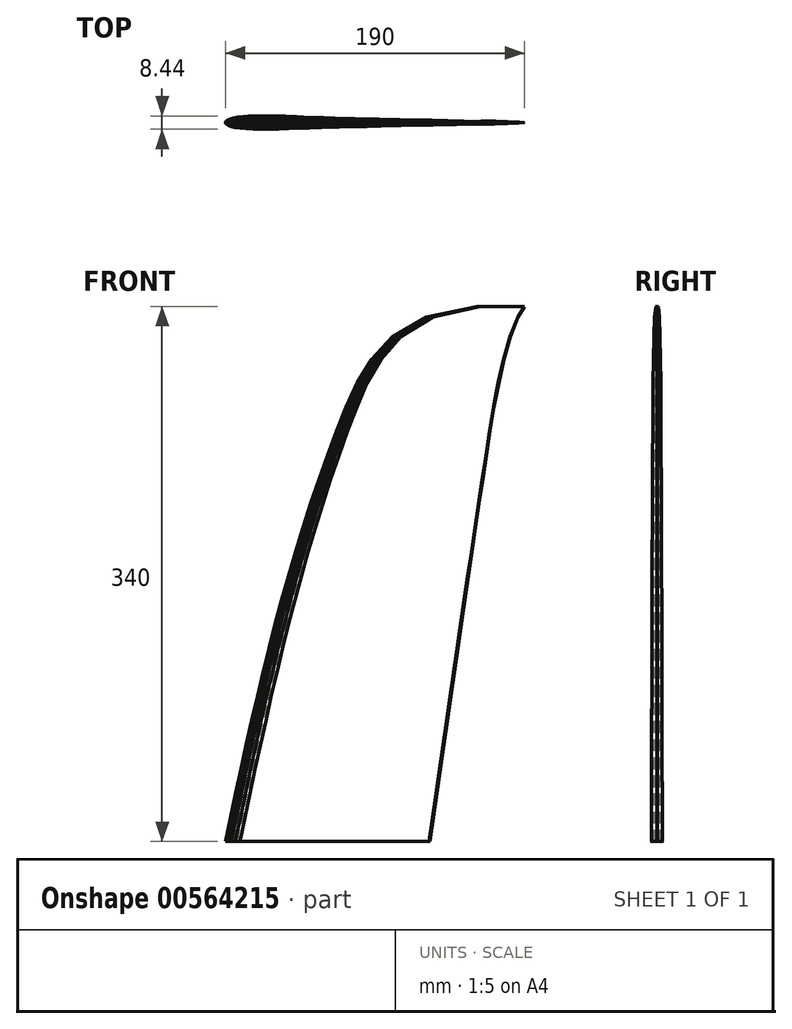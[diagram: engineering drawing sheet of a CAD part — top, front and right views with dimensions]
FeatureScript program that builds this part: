
annotation { "Feature Type Name" : "Feature", "Feature Type Description" : "" }
export const myFeature = defineFeature(function(context is Context, id is Id, definition is map)
    precondition{}
    {
        {
            var Q0;
            Q0=qCreatedBy(makeId("Top.planeOp"),FACE);
            cPlane(context, id + "F0", {"entities" : qUnion([Q0]), "cplaneType" : CPlaneType.OFFSET, "offset" : 250 * mm, "width" : 150 * mm, "height" : 150 * mm});
        }
        {
            var Q0;
            Q0=qCreatedBy(makeId("Top.planeOp"),FACE);
            cPlane(context, id + "F1", {"entities" : qUnion([Q0]), "cplaneType" : CPlaneType.OFFSET, "offset" : 300 * mm, "width" : 150 * mm, "height" : 150 * mm});
        }
        {
            var Q0;
            Q0=qCreatedBy(makeId("Top.planeOp"),FACE);
            cPlane(context, id + "F2", {"entities" : qUnion([Q0]), "cplaneType" : CPlaneType.OFFSET, "offset" : 320 * mm, "width" : 150 * mm, "height" : 150 * mm});
        }
        {
            var Q0;
            Q0=qCreatedBy(makeId("Top.planeOp"),FACE);
            cPlane(context, id + "F3", {"entities" : qUnion([Q0]), "cplaneType" : CPlaneType.OFFSET, "offset" : 340 * mm, "width" : 150 * mm, "height" : 150 * mm});
        }
        {
            var Q0;
            Q0=qCreatedBy(makeId("Top.planeOp"),FACE);
            var sketch = newSketch(context, id + "F4", { "sketchPlane" : qUnion([Q0])});
            skLineSegment(sketch, "E0", {"start": v(130, 0.16) * mm, "end": v(129.46, 0.15) * mm});
            skLineSegment(sketch, "E1", {"start": v(129.46, 0.15) * mm, "end": v(128.28, 0.22) * mm});
            skLineSegment(sketch, "E2", {"start": v(128.28, 0.22) * mm, "end": v(126.06, 0.3) * mm});
            skLineSegment(sketch, "E3", {"start": v(126.06, 0.3) * mm, "end": v(123.2, 0.44) * mm});
            skLineSegment(sketch, "E4", {"start": v(123.2, 0.44) * mm, "end": v(119.45, 0.6) * mm});
            skLineSegment(sketch, "E5", {"start": v(119.45, 0.6) * mm, "end": v(115.33, 0.75) * mm});
            skLineSegment(sketch, "E6", {"start": v(115.33, 0.75) * mm, "end": v(110.89, 0.96) * mm});
            skLineSegment(sketch, "E7", {"start": v(110.89, 0.96) * mm, "end": v(106, 1.14) * mm});
            skLineSegment(sketch, "E8", {"start": v(106, 1.14) * mm, "end": v(100.37, 1.42) * mm});
            skLineSegment(sketch, "E9", {"start": v(100.37, 1.42) * mm, "end": v(94.84, 1.6) * mm});
            skLineSegment(sketch, "E10", {"start": v(94.84, 1.6) * mm, "end": v(89.05, 1.89) * mm});
            skLineSegment(sketch, "E11", {"start": v(89.05, 1.89) * mm, "end": v(82.47, 2.15) * mm});
            skLineSegment(sketch, "E12", {"start": v(82.47, 2.15) * mm, "end": v(76.13, 2.4) * mm});
            skLineSegment(sketch, "E13", {"start": v(76.13, 2.4) * mm, "end": v(69.53, 2.68) * mm});
            skLineSegment(sketch, "E14", {"start": v(69.53, 2.68) * mm, "end": v(62.6, 3.03) * mm});
            skLineSegment(sketch, "E15", {"start": v(62.6, 3.03) * mm, "end": v(56.55, 3.26) * mm});
            skLineSegment(sketch, "E16", {"start": v(56.55, 3.26) * mm, "end": v(49.78, 3.57) * mm});
            skLineSegment(sketch, "E17", {"start": v(49.78, 3.57) * mm, "end": v(45.16, 3.74) * mm});
            skLineSegment(sketch, "E18", {"start": v(45.16, 3.74) * mm, "end": v(38.39, 3.98) * mm});
            skLineSegment(sketch, "E19", {"start": v(38.39, 3.98) * mm, "end": v(33.66, 4.1) * mm});
            skLineSegment(sketch, "E20", {"start": v(33.66, 4.1) * mm, "end": v(28.01, 4.2) * mm});
            skLineSegment(sketch, "E21", {"start": v(28.01, 4.2) * mm, "end": v(23.16, 4.22) * mm});
            skLineSegment(sketch, "E22", {"start": v(23.16, 4.22) * mm, "end": v(18.3, 4.15) * mm});
            skLineSegment(sketch, "E23", {"start": v(18.3, 4.15) * mm, "end": v(14.57, 4) * mm});
            skLineSegment(sketch, "E24", {"start": v(14.57, 4) * mm, "end": v(11.21, 3.75) * mm});
            skLineSegment(sketch, "E25", {"start": v(11.21, 3.75) * mm, "end": v(7.63, 3.34) * mm});
            skLineSegment(sketch, "E26", {"start": v(7.63, 3.34) * mm, "end": v(5.05, 2.89) * mm});
            skLineSegment(sketch, "E27", {"start": v(5.05, 2.89) * mm, "end": v(2.92, 2.28) * mm});
            skLineSegment(sketch, "E28", {"start": v(2.92, 2.28) * mm, "end": v(1.32, 1.56) * mm});
            skLineSegment(sketch, "E29", {"start": v(1.32, 1.56) * mm, "end": v(0.49, 0.98) * mm});
            skLineSegment(sketch, "E30", {"start": v(0.49, 0.98) * mm, "end": v(0.08, 0.4) * mm});
            skLineSegment(sketch, "E31", {"start": v(0.08, 0.4) * mm, "end": v(0, 0) * mm});
            skLineSegment(sketch, "E32", {"start": v(0, 0) * mm, "end": v(0.03, -0.22) * mm});
            skLineSegment(sketch, "E33", {"start": v(0.03, -0.22) * mm, "end": v(0.08, -0.45) * mm});
            skLineSegment(sketch, "E34", {"start": v(0.08, -0.45) * mm, "end": v(0.22, -0.67) * mm});
            skLineSegment(sketch, "E35", {"start": v(0.22, -0.67) * mm, "end": v(1, -1.38) * mm});
            skLineSegment(sketch, "E36", {"start": v(1, -1.38) * mm, "end": v(2.07, -1.93) * mm});
            skLineSegment(sketch, "E37", {"start": v(2.07, -1.93) * mm, "end": v(3.73, -2.53) * mm});
            skLineSegment(sketch, "E38", {"start": v(3.73, -2.53) * mm, "end": v(6.34, -3.13) * mm});
            skLineSegment(sketch, "E39", {"start": v(6.34, -3.13) * mm, "end": v(9.36, -3.57) * mm});
            skLineSegment(sketch, "E40", {"start": v(9.36, -3.57) * mm, "end": v(13.18, -3.91) * mm});
            skLineSegment(sketch, "E41", {"start": v(13.18, -3.91) * mm, "end": v(17.57, -4.14) * mm});
            skLineSegment(sketch, "E42", {"start": v(17.57, -4.14) * mm, "end": v(22.67, -4.2) * mm});
            skLineSegment(sketch, "E43", {"start": v(22.67, -4.2) * mm, "end": v(28.18, -4.22) * mm});
            skLineSegment(sketch, "E44", {"start": v(28.18, -4.22) * mm, "end": v(34.02, -4.06) * mm});
            skLineSegment(sketch, "E45", {"start": v(34.02, -4.06) * mm, "end": v(40.18, -3.88) * mm});
            skLineSegment(sketch, "E46", {"start": v(40.18, -3.88) * mm, "end": v(46.73, -3.67) * mm});
            skLineSegment(sketch, "E47", {"start": v(46.73, -3.67) * mm, "end": v(53.52, -3.4) * mm});
            skLineSegment(sketch, "E48", {"start": v(53.52, -3.4) * mm, "end": v(61.2, -3.04) * mm});
            skLineSegment(sketch, "E49", {"start": v(61.2, -3.04) * mm, "end": v(67.7, -2.76) * mm});
            skLineSegment(sketch, "E50", {"start": v(67.7, -2.76) * mm, "end": v(74.25, -2.49) * mm});
            skLineSegment(sketch, "E51", {"start": v(74.25, -2.49) * mm, "end": v(81.45, -2.17) * mm});
            skLineSegment(sketch, "E52", {"start": v(81.45, -2.17) * mm, "end": v(88.16, -1.9) * mm});
            skLineSegment(sketch, "E53", {"start": v(88.16, -1.9) * mm, "end": v(94.61, -1.62) * mm});
            skLineSegment(sketch, "E54", {"start": v(94.61, -1.62) * mm, "end": v(100.76, -1.37) * mm});
            skLineSegment(sketch, "E55", {"start": v(100.76, -1.37) * mm, "end": v(106.42, -1.13) * mm});
            skLineSegment(sketch, "E56", {"start": v(106.42, -1.13) * mm, "end": v(111.7, -0.9) * mm});
            skLineSegment(sketch, "E57", {"start": v(111.7, -0.9) * mm, "end": v(116.1, -0.72) * mm});
            skLineSegment(sketch, "E58", {"start": v(116.1, -0.72) * mm, "end": v(120.1, -0.54) * mm});
            skLineSegment(sketch, "E59", {"start": v(120.1, -0.54) * mm, "end": v(123.41, -0.43) * mm});
            skLineSegment(sketch, "E60", {"start": v(123.41, -0.43) * mm, "end": v(126.23, -0.29) * mm});
            skLineSegment(sketch, "E61", {"start": v(126.23, -0.29) * mm, "end": v(128.2, -0.2) * mm});
            skLineSegment(sketch, "E62", {"start": v(128.2, -0.2) * mm, "end": v(130, -0.13) * mm});
            skLineSegment(sketch, "E63", {"start": v(130, -0.13) * mm, "end": v(130, 0.16) * mm});
            skSolve(sketch);
        }
        {
            var Q0;
            Q0=qCreatedBy(id+"F0.planeOp",FACE);
            var sketch = newSketch(context, id + "F5", { "sketchPlane" : qUnion([Q0])});
            skLineSegment(sketch, "E64", {"start": v(166.6, 0.13) * mm, "end": v(166.18, 0.12) * mm});
            skLineSegment(sketch, "E65", {"start": v(166.18, 0.12) * mm, "end": v(165.27, 0.17) * mm});
            skLineSegment(sketch, "E66", {"start": v(165.27, 0.17) * mm, "end": v(163.56, 0.23) * mm});
            skLineSegment(sketch, "E67", {"start": v(163.56, 0.23) * mm, "end": v(161.37, 0.33) * mm});
            skLineSegment(sketch, "E68", {"start": v(161.37, 0.33) * mm, "end": v(158.49, 0.46) * mm});
            skLineSegment(sketch, "E69", {"start": v(158.49, 0.46) * mm, "end": v(155.31, 0.58) * mm});
            skLineSegment(sketch, "E70", {"start": v(155.31, 0.58) * mm, "end": v(151.9, 0.74) * mm});
            skLineSegment(sketch, "E71", {"start": v(151.9, 0.74) * mm, "end": v(148.14, 0.88) * mm});
            skLineSegment(sketch, "E72", {"start": v(148.14, 0.88) * mm, "end": v(143.8, 1.1) * mm});
            skLineSegment(sketch, "E73", {"start": v(143.8, 1.1) * mm, "end": v(139.55, 1.24) * mm});
            skLineSegment(sketch, "E74", {"start": v(139.55, 1.24) * mm, "end": v(135.1, 1.45) * mm});
            skLineSegment(sketch, "E75", {"start": v(135.1, 1.45) * mm, "end": v(130.04, 1.65) * mm});
            skLineSegment(sketch, "E76", {"start": v(130.04, 1.65) * mm, "end": v(125.16, 1.85) * mm});
            skLineSegment(sketch, "E77", {"start": v(125.16, 1.85) * mm, "end": v(120.08, 2.06) * mm});
            skLineSegment(sketch, "E78", {"start": v(120.08, 2.06) * mm, "end": v(114.76, 2.33) * mm});
            skLineSegment(sketch, "E79", {"start": v(114.76, 2.33) * mm, "end": v(110.1, 2.5) * mm});
            skLineSegment(sketch, "E80", {"start": v(110.1, 2.5) * mm, "end": v(104.9, 2.75) * mm});
            skLineSegment(sketch, "E81", {"start": v(104.9, 2.75) * mm, "end": v(101.34, 2.88) * mm});
            skLineSegment(sketch, "E82", {"start": v(101.34, 2.88) * mm, "end": v(96.13, 3.06) * mm});
            skLineSegment(sketch, "E83", {"start": v(96.13, 3.06) * mm, "end": v(92.5, 3.16) * mm});
            skLineSegment(sketch, "E84", {"start": v(92.5, 3.16) * mm, "end": v(88.15, 3.23) * mm});
            skLineSegment(sketch, "E85", {"start": v(88.15, 3.23) * mm, "end": v(84.42, 3.24) * mm});
            skLineSegment(sketch, "E86", {"start": v(84.42, 3.24) * mm, "end": v(80.69, 3.19) * mm});
            skLineSegment(sketch, "E87", {"start": v(80.69, 3.19) * mm, "end": v(77.81, 3.08) * mm});
            skLineSegment(sketch, "E88", {"start": v(77.81, 3.08) * mm, "end": v(75.23, 2.89) * mm});
            skLineSegment(sketch, "E89", {"start": v(75.23, 2.89) * mm, "end": v(72.47, 2.57) * mm});
            skLineSegment(sketch, "E90", {"start": v(72.47, 2.57) * mm, "end": v(70.5, 2.22) * mm});
            skLineSegment(sketch, "E91", {"start": v(70.5, 2.22) * mm, "end": v(68.85, 1.76) * mm});
            skLineSegment(sketch, "E92", {"start": v(68.85, 1.76) * mm, "end": v(67.62, 1.2) * mm});
            skLineSegment(sketch, "E93", {"start": v(67.62, 1.2) * mm, "end": v(66.98, 0.75) * mm});
            skLineSegment(sketch, "E94", {"start": v(66.98, 0.75) * mm, "end": v(66.66, 0.3) * mm});
            skLineSegment(sketch, "E95", {"start": v(66.66, 0.3) * mm, "end": v(66.6, 0) * mm});
            skLineSegment(sketch, "E96", {"start": v(66.6, 0) * mm, "end": v(66.62, -0.17) * mm});
            skLineSegment(sketch, "E97", {"start": v(66.62, -0.17) * mm, "end": v(66.66, -0.35) * mm});
            skLineSegment(sketch, "E98", {"start": v(66.66, -0.35) * mm, "end": v(66.78, -0.52) * mm});
            skLineSegment(sketch, "E99", {"start": v(66.78, -0.52) * mm, "end": v(67.37, -1.06) * mm});
            skLineSegment(sketch, "E100", {"start": v(67.37, -1.06) * mm, "end": v(68.2, -1.48) * mm});
            skLineSegment(sketch, "E101", {"start": v(68.2, -1.48) * mm, "end": v(69.47, -1.95) * mm});
            skLineSegment(sketch, "E102", {"start": v(69.47, -1.95) * mm, "end": v(71.48, -2.4) * mm});
            skLineSegment(sketch, "E103", {"start": v(71.48, -2.4) * mm, "end": v(73.8, -2.74) * mm});
            skLineSegment(sketch, "E104", {"start": v(73.8, -2.74) * mm, "end": v(76.75, -3) * mm});
            skLineSegment(sketch, "E105", {"start": v(76.75, -3) * mm, "end": v(80.12, -3.18) * mm});
            skLineSegment(sketch, "E106", {"start": v(80.12, -3.18) * mm, "end": v(84.04, -3.23) * mm});
            skLineSegment(sketch, "E107", {"start": v(84.04, -3.23) * mm, "end": v(88.28, -3.24) * mm});
            skLineSegment(sketch, "E108", {"start": v(88.28, -3.24) * mm, "end": v(92.77, -3.12) * mm});
            skLineSegment(sketch, "E109", {"start": v(92.77, -3.12) * mm, "end": v(97.5, -2.99) * mm});
            skLineSegment(sketch, "E110", {"start": v(97.5, -2.99) * mm, "end": v(102.55, -2.82) * mm});
            skLineSegment(sketch, "E111", {"start": v(102.55, -2.82) * mm, "end": v(107.77, -2.62) * mm});
            skLineSegment(sketch, "E112", {"start": v(107.77, -2.62) * mm, "end": v(113.67, -2.34) * mm});
            skLineSegment(sketch, "E113", {"start": v(113.67, -2.34) * mm, "end": v(118.68, -2.12) * mm});
            skLineSegment(sketch, "E114", {"start": v(118.68, -2.12) * mm, "end": v(123.72, -1.91) * mm});
            skLineSegment(sketch, "E115", {"start": v(123.72, -1.91) * mm, "end": v(129.25, -1.67) * mm});
            skLineSegment(sketch, "E116", {"start": v(129.25, -1.67) * mm, "end": v(134.41, -1.46) * mm});
            skLineSegment(sketch, "E117", {"start": v(134.41, -1.46) * mm, "end": v(139.38, -1.24) * mm});
            skLineSegment(sketch, "E118", {"start": v(139.38, -1.24) * mm, "end": v(144.1, -1.06) * mm});
            skLineSegment(sketch, "E119", {"start": v(144.1, -1.06) * mm, "end": v(148.46, -0.87) * mm});
            skLineSegment(sketch, "E120", {"start": v(148.46, -0.87) * mm, "end": v(152.52, -0.7) * mm});
            skLineSegment(sketch, "E121", {"start": v(152.52, -0.7) * mm, "end": v(155.91, -0.56) * mm});
            skLineSegment(sketch, "E122", {"start": v(155.91, -0.56) * mm, "end": v(158.99, -0.42) * mm});
            skLineSegment(sketch, "E123", {"start": v(158.99, -0.42) * mm, "end": v(161.53, -0.33) * mm});
            skLineSegment(sketch, "E124", {"start": v(161.53, -0.33) * mm, "end": v(163.7, -0.22) * mm});
            skLineSegment(sketch, "E125", {"start": v(163.7, -0.22) * mm, "end": v(165.2, -0.15) * mm});
            skLineSegment(sketch, "E126", {"start": v(165.2, -0.15) * mm, "end": v(166.6, -0.1) * mm});
            skLineSegment(sketch, "E127", {"start": v(166.6, -0.1) * mm, "end": v(166.6, 0.13) * mm});
            skSolve(sketch);
        }
        {
            var Q0;
            Q0=qCreatedBy(id+"F1.planeOp",FACE);
            var sketch = newSketch(context, id + "F6", { "sketchPlane" : qUnion([Q0])});
            skLineSegment(sketch, "E128", {"start": v(175.53, 0.1) * mm, "end": v(175.16, 0.1) * mm});
            skLineSegment(sketch, "E129", {"start": v(175.16, 0.1) * mm, "end": v(174.37, 0.15) * mm});
            skLineSegment(sketch, "E130", {"start": v(174.37, 0.15) * mm, "end": v(172.88, 0.2) * mm});
            skLineSegment(sketch, "E131", {"start": v(172.88, 0.2) * mm, "end": v(170.98, 0.3) * mm});
            skLineSegment(sketch, "E132", {"start": v(170.98, 0.3) * mm, "end": v(168.46, 0.4) * mm});
            skLineSegment(sketch, "E133", {"start": v(168.46, 0.4) * mm, "end": v(165.7, 0.5) * mm});
            skLineSegment(sketch, "E134", {"start": v(165.7, 0.5) * mm, "end": v(162.73, 0.64) * mm});
            skLineSegment(sketch, "E135", {"start": v(162.73, 0.64) * mm, "end": v(159.46, 0.76) * mm});
            skLineSegment(sketch, "E136", {"start": v(159.46, 0.76) * mm, "end": v(155.68, 0.95) * mm});
            skLineSegment(sketch, "E137", {"start": v(155.68, 0.95) * mm, "end": v(151.98, 1.08) * mm});
            skLineSegment(sketch, "E138", {"start": v(151.98, 1.08) * mm, "end": v(148.1, 1.26) * mm});
            skLineSegment(sketch, "E139", {"start": v(148.1, 1.26) * mm, "end": v(143.7, 1.44) * mm});
            skLineSegment(sketch, "E140", {"start": v(143.7, 1.44) * mm, "end": v(139.45, 1.61) * mm});
            skLineSegment(sketch, "E141", {"start": v(139.45, 1.61) * mm, "end": v(135.03, 1.8) * mm});
            skLineSegment(sketch, "E142", {"start": v(135.03, 1.8) * mm, "end": v(130.4, 2.03) * mm});
            skLineSegment(sketch, "E143", {"start": v(130.4, 2.03) * mm, "end": v(126.34, 2.18) * mm});
            skLineSegment(sketch, "E144", {"start": v(126.34, 2.18) * mm, "end": v(121.81, 2.4) * mm});
            skLineSegment(sketch, "E145", {"start": v(121.81, 2.4) * mm, "end": v(118.72, 2.5) * mm});
            skLineSegment(sketch, "E146", {"start": v(118.72, 2.5) * mm, "end": v(114.18, 2.66) * mm});
            skLineSegment(sketch, "E147", {"start": v(114.18, 2.66) * mm, "end": v(111.02, 2.75) * mm});
            skLineSegment(sketch, "E148", {"start": v(111.02, 2.75) * mm, "end": v(107.23, 2.81) * mm});
            skLineSegment(sketch, "E149", {"start": v(107.23, 2.81) * mm, "end": v(103.99, 2.82) * mm});
            skLineSegment(sketch, "E150", {"start": v(103.99, 2.82) * mm, "end": v(100.74, 2.78) * mm});
            skLineSegment(sketch, "E151", {"start": v(100.74, 2.78) * mm, "end": v(98.23, 2.68) * mm});
            skLineSegment(sketch, "E152", {"start": v(98.23, 2.68) * mm, "end": v(95.99, 2.51) * mm});
            skLineSegment(sketch, "E153", {"start": v(95.99, 2.51) * mm, "end": v(93.58, 2.24) * mm});
            skLineSegment(sketch, "E154", {"start": v(93.58, 2.24) * mm, "end": v(91.86, 1.93) * mm});
            skLineSegment(sketch, "E155", {"start": v(91.86, 1.93) * mm, "end": v(90.43, 1.53) * mm});
            skLineSegment(sketch, "E156", {"start": v(90.43, 1.53) * mm, "end": v(89.36, 1.04) * mm});
            skLineSegment(sketch, "E157", {"start": v(89.36, 1.04) * mm, "end": v(88.8, 0.65) * mm});
            skLineSegment(sketch, "E158", {"start": v(88.8, 0.65) * mm, "end": v(88.53, 0.27) * mm});
            skLineSegment(sketch, "E159", {"start": v(88.53, 0.27) * mm, "end": v(88.47, 0) * mm});
            skLineSegment(sketch, "E160", {"start": v(88.47, 0) * mm, "end": v(88.5, -0.15) * mm});
            skLineSegment(sketch, "E161", {"start": v(88.5, -0.15) * mm, "end": v(88.53, -0.3) * mm});
            skLineSegment(sketch, "E162", {"start": v(88.53, -0.3) * mm, "end": v(88.63, -0.45) * mm});
            skLineSegment(sketch, "E163", {"start": v(88.63, -0.45) * mm, "end": v(89.14, -0.93) * mm});
            skLineSegment(sketch, "E164", {"start": v(89.14, -0.93) * mm, "end": v(89.86, -1.3) * mm});
            skLineSegment(sketch, "E165", {"start": v(89.86, -1.3) * mm, "end": v(90.98, -1.7) * mm});
            skLineSegment(sketch, "E166", {"start": v(90.98, -1.7) * mm, "end": v(92.72, -2.1) * mm});
            skLineSegment(sketch, "E167", {"start": v(92.72, -2.1) * mm, "end": v(94.75, -2.39) * mm});
            skLineSegment(sketch, "E168", {"start": v(94.75, -2.39) * mm, "end": v(97.3, -2.62) * mm});
            skLineSegment(sketch, "E169", {"start": v(97.3, -2.62) * mm, "end": v(100.24, -2.77) * mm});
            skLineSegment(sketch, "E170", {"start": v(100.24, -2.77) * mm, "end": v(103.66, -2.8) * mm});
            skLineSegment(sketch, "E171", {"start": v(103.66, -2.8) * mm, "end": v(107.34, -2.82) * mm});
            skLineSegment(sketch, "E172", {"start": v(107.34, -2.82) * mm, "end": v(111.26, -2.72) * mm});
            skLineSegment(sketch, "E173", {"start": v(111.26, -2.72) * mm, "end": v(115.38, -2.6) * mm});
            skLineSegment(sketch, "E174", {"start": v(115.38, -2.6) * mm, "end": v(119.77, -2.46) * mm});
            skLineSegment(sketch, "E175", {"start": v(119.77, -2.46) * mm, "end": v(124.31, -2.28) * mm});
            skLineSegment(sketch, "E176", {"start": v(124.31, -2.28) * mm, "end": v(129.45, -2.03) * mm});
            skLineSegment(sketch, "E177", {"start": v(129.45, -2.03) * mm, "end": v(133.81, -1.85) * mm});
            skLineSegment(sketch, "E178", {"start": v(133.81, -1.85) * mm, "end": v(138.2, -1.66) * mm});
            skLineSegment(sketch, "E179", {"start": v(138.2, -1.66) * mm, "end": v(143.02, -1.45) * mm});
            skLineSegment(sketch, "E180", {"start": v(143.02, -1.45) * mm, "end": v(147.5, -1.28) * mm});
            skLineSegment(sketch, "E181", {"start": v(147.5, -1.28) * mm, "end": v(151.83, -1.08) * mm});
            skLineSegment(sketch, "E182", {"start": v(151.83, -1.08) * mm, "end": v(155.95, -0.92) * mm});
            skLineSegment(sketch, "E183", {"start": v(155.95, -0.92) * mm, "end": v(159.74, -0.76) * mm});
            skLineSegment(sketch, "E184", {"start": v(159.74, -0.76) * mm, "end": v(163.27, -0.6) * mm});
            skLineSegment(sketch, "E185", {"start": v(163.27, -0.6) * mm, "end": v(166.22, -0.48) * mm});
            skLineSegment(sketch, "E186", {"start": v(166.22, -0.48) * mm, "end": v(168.9, -0.36) * mm});
            skLineSegment(sketch, "E187", {"start": v(168.9, -0.36) * mm, "end": v(171.11, -0.29) * mm});
            skLineSegment(sketch, "E188", {"start": v(171.11, -0.29) * mm, "end": v(173, -0.2) * mm});
            skLineSegment(sketch, "E189", {"start": v(173, -0.2) * mm, "end": v(174.32, -0.13) * mm});
            skLineSegment(sketch, "E190", {"start": v(174.32, -0.13) * mm, "end": v(175.53, -0.09) * mm});
            skLineSegment(sketch, "E191", {"start": v(175.53, -0.09) * mm, "end": v(175.53, 0.1) * mm});
            skSolve(sketch);
        }
        {
            var Q0;
            Q0=qCreatedBy(id+"F2.planeOp",FACE);
            var sketch = newSketch(context, id + "F7", { "sketchPlane" : qUnion([Q0])});
            skLineSegment(sketch, "E192", {"start": v(180.66, 0.1) * mm, "end": v(180.34, 0.09) * mm});
            skLineSegment(sketch, "E193", {"start": v(180.34, 0.09) * mm, "end": v(179.66, 0.13) * mm});
            skLineSegment(sketch, "E194", {"start": v(179.66, 0.13) * mm, "end": v(178.37, 0.17) * mm});
            skLineSegment(sketch, "E195", {"start": v(178.37, 0.17) * mm, "end": v(176.72, 0.25) * mm});
            skLineSegment(sketch, "E196", {"start": v(176.72, 0.25) * mm, "end": v(174.55, 0.34) * mm});
            skLineSegment(sketch, "E197", {"start": v(174.55, 0.34) * mm, "end": v(172.16, 0.44) * mm});
            skLineSegment(sketch, "E198", {"start": v(172.16, 0.44) * mm, "end": v(169.58, 0.55) * mm});
            skLineSegment(sketch, "E199", {"start": v(169.58, 0.55) * mm, "end": v(166.75, 0.66) * mm});
            skLineSegment(sketch, "E200", {"start": v(166.75, 0.66) * mm, "end": v(163.49, 0.82) * mm});
            skLineSegment(sketch, "E201", {"start": v(163.49, 0.82) * mm, "end": v(160.28, 0.93) * mm});
            skLineSegment(sketch, "E202", {"start": v(160.28, 0.93) * mm, "end": v(156.93, 1.1) * mm});
            skLineSegment(sketch, "E203", {"start": v(156.93, 1.1) * mm, "end": v(153.12, 1.25) * mm});
            skLineSegment(sketch, "E204", {"start": v(153.12, 1.25) * mm, "end": v(149.45, 1.4) * mm});
            skLineSegment(sketch, "E205", {"start": v(149.45, 1.4) * mm, "end": v(145.62, 1.55) * mm});
            skLineSegment(sketch, "E206", {"start": v(145.62, 1.55) * mm, "end": v(141.61, 1.76) * mm});
            skLineSegment(sketch, "E207", {"start": v(141.61, 1.76) * mm, "end": v(138.1, 1.89) * mm});
            skLineSegment(sketch, "E208", {"start": v(138.1, 1.89) * mm, "end": v(134.19, 2.07) * mm});
            skLineSegment(sketch, "E209", {"start": v(134.19, 2.07) * mm, "end": v(131.5, 2.17) * mm});
            skLineSegment(sketch, "E210", {"start": v(131.5, 2.17) * mm, "end": v(127.58, 2.3) * mm});
            skLineSegment(sketch, "E211", {"start": v(127.58, 2.3) * mm, "end": v(124.85, 2.38) * mm});
            skLineSegment(sketch, "E212", {"start": v(124.85, 2.38) * mm, "end": v(121.57, 2.43) * mm});
            skLineSegment(sketch, "E213", {"start": v(121.57, 2.43) * mm, "end": v(118.76, 2.44) * mm});
            skLineSegment(sketch, "E214", {"start": v(118.76, 2.44) * mm, "end": v(115.95, 2.4) * mm});
            skLineSegment(sketch, "E215", {"start": v(115.95, 2.4) * mm, "end": v(113.79, 2.32) * mm});
            skLineSegment(sketch, "E216", {"start": v(113.79, 2.32) * mm, "end": v(111.84, 2.17) * mm});
            skLineSegment(sketch, "E217", {"start": v(111.84, 2.17) * mm, "end": v(109.76, 1.93) * mm});
            skLineSegment(sketch, "E218", {"start": v(109.76, 1.93) * mm, "end": v(108.27, 1.67) * mm});
            skLineSegment(sketch, "E219", {"start": v(108.27, 1.67) * mm, "end": v(107.04, 1.32) * mm});
            skLineSegment(sketch, "E220", {"start": v(107.04, 1.32) * mm, "end": v(106.1, 0.9) * mm});
            skLineSegment(sketch, "E221", {"start": v(106.1, 0.9) * mm, "end": v(105.63, 0.57) * mm});
            skLineSegment(sketch, "E222", {"start": v(105.63, 0.57) * mm, "end": v(105.39, 0.23) * mm});
            skLineSegment(sketch, "E223", {"start": v(105.39, 0.23) * mm, "end": v(105.34, 0) * mm});
            skLineSegment(sketch, "E224", {"start": v(105.34, 0) * mm, "end": v(105.36, -0.13) * mm});
            skLineSegment(sketch, "E225", {"start": v(105.36, -0.13) * mm, "end": v(105.39, -0.26) * mm});
            skLineSegment(sketch, "E226", {"start": v(105.39, -0.26) * mm, "end": v(105.47, -0.39) * mm});
            skLineSegment(sketch, "E227", {"start": v(105.47, -0.39) * mm, "end": v(105.92, -0.8) * mm});
            skLineSegment(sketch, "E228", {"start": v(105.92, -0.8) * mm, "end": v(106.54, -1.12) * mm});
            skLineSegment(sketch, "E229", {"start": v(106.54, -1.12) * mm, "end": v(107.5, -1.47) * mm});
            skLineSegment(sketch, "E230", {"start": v(107.5, -1.47) * mm, "end": v(109.02, -1.81) * mm});
            skLineSegment(sketch, "E231", {"start": v(109.02, -1.81) * mm, "end": v(110.77, -2.07) * mm});
            skLineSegment(sketch, "E232", {"start": v(110.77, -2.07) * mm, "end": v(112.98, -2.27) * mm});
            skLineSegment(sketch, "E233", {"start": v(112.98, -2.27) * mm, "end": v(115.52, -2.4) * mm});
            skLineSegment(sketch, "E234", {"start": v(115.52, -2.4) * mm, "end": v(118.48, -2.43) * mm});
            skLineSegment(sketch, "E235", {"start": v(118.48, -2.43) * mm, "end": v(121.67, -2.44) * mm});
            skLineSegment(sketch, "E236", {"start": v(121.67, -2.44) * mm, "end": v(125.06, -2.35) * mm});
            skLineSegment(sketch, "E237", {"start": v(125.06, -2.35) * mm, "end": v(128.62, -2.25) * mm});
            skLineSegment(sketch, "E238", {"start": v(128.62, -2.25) * mm, "end": v(132.42, -2.13) * mm});
            skLineSegment(sketch, "E239", {"start": v(132.42, -2.13) * mm, "end": v(136.35, -1.97) * mm});
            skLineSegment(sketch, "E240", {"start": v(136.35, -1.97) * mm, "end": v(140.8, -1.76) * mm});
            skLineSegment(sketch, "E241", {"start": v(140.8, -1.76) * mm, "end": v(144.57, -1.6) * mm});
            skLineSegment(sketch, "E242", {"start": v(144.57, -1.6) * mm, "end": v(148.36, -1.44) * mm});
            skLineSegment(sketch, "E243", {"start": v(148.36, -1.44) * mm, "end": v(152.53, -1.26) * mm});
            skLineSegment(sketch, "E244", {"start": v(152.53, -1.26) * mm, "end": v(156.41, -1.1) * mm});
            skLineSegment(sketch, "E245", {"start": v(156.41, -1.1) * mm, "end": v(160.16, -0.94) * mm});
            skLineSegment(sketch, "E246", {"start": v(160.16, -0.94) * mm, "end": v(163.72, -0.8) * mm});
            skLineSegment(sketch, "E247", {"start": v(163.72, -0.8) * mm, "end": v(167, -0.65) * mm});
            skLineSegment(sketch, "E248", {"start": v(167, -0.65) * mm, "end": v(170.05, -0.53) * mm});
            skLineSegment(sketch, "E249", {"start": v(170.05, -0.53) * mm, "end": v(172.6, -0.42) * mm});
            skLineSegment(sketch, "E250", {"start": v(172.6, -0.42) * mm, "end": v(174.92, -0.31) * mm});
            skLineSegment(sketch, "E251", {"start": v(174.92, -0.31) * mm, "end": v(176.84, -0.25) * mm});
            skLineSegment(sketch, "E252", {"start": v(176.84, -0.25) * mm, "end": v(178.47, -0.17) * mm});
            skLineSegment(sketch, "E253", {"start": v(178.47, -0.17) * mm, "end": v(179.61, -0.12) * mm});
            skLineSegment(sketch, "E254", {"start": v(179.61, -0.12) * mm, "end": v(180.66, -0.08) * mm});
            skLineSegment(sketch, "E255", {"start": v(180.66, -0.08) * mm, "end": v(180.66, 0.1) * mm});
            skSolve(sketch);
        }
        {
            var Q0;
            Q0=qCreatedBy(id+"F3.planeOp",FACE);
            var sketch = newSketch(context, id + "F8", { "sketchPlane" : qUnion([Q0])});
            skLineSegment(sketch, "E256", {"start": v(190, 0.04) * mm, "end": v(189.88, 0.03) * mm});
            skLineSegment(sketch, "E257", {"start": v(189.88, 0.03) * mm, "end": v(189.6, 0.05) * mm});
            skLineSegment(sketch, "E258", {"start": v(189.6, 0.05) * mm, "end": v(189.1, 0.07) * mm});
            skLineSegment(sketch, "E259", {"start": v(189.1, 0.07) * mm, "end": v(188.44, 0.1) * mm});
            skLineSegment(sketch, "E260", {"start": v(188.44, 0.1) * mm, "end": v(187.57, 0.14) * mm});
            skLineSegment(sketch, "E261", {"start": v(187.57, 0.14) * mm, "end": v(186.62, 0.17) * mm});
            skLineSegment(sketch, "E262", {"start": v(186.62, 0.17) * mm, "end": v(185.6, 0.22) * mm});
            skLineSegment(sketch, "E263", {"start": v(185.6, 0.22) * mm, "end": v(184.46, 0.26) * mm});
            skLineSegment(sketch, "E264", {"start": v(184.46, 0.26) * mm, "end": v(183.16, 0.33) * mm});
            skLineSegment(sketch, "E265", {"start": v(183.16, 0.33) * mm, "end": v(181.89, 0.37) * mm});
            skLineSegment(sketch, "E266", {"start": v(181.89, 0.37) * mm, "end": v(180.55, 0.44) * mm});
            skLineSegment(sketch, "E267", {"start": v(180.55, 0.44) * mm, "end": v(179.03, 0.5) * mm});
            skLineSegment(sketch, "E268", {"start": v(179.03, 0.5) * mm, "end": v(177.57, 0.56) * mm});
            skLineSegment(sketch, "E269", {"start": v(177.57, 0.56) * mm, "end": v(176.05, 0.62) * mm});
            skLineSegment(sketch, "E270", {"start": v(176.05, 0.62) * mm, "end": v(174.45, 0.7) * mm});
            skLineSegment(sketch, "E271", {"start": v(174.45, 0.7) * mm, "end": v(173.05, 0.75) * mm});
            skLineSegment(sketch, "E272", {"start": v(173.05, 0.75) * mm, "end": v(171.49, 0.82) * mm});
            skLineSegment(sketch, "E273", {"start": v(171.49, 0.82) * mm, "end": v(170.42, 0.86) * mm});
            skLineSegment(sketch, "E274", {"start": v(170.42, 0.86) * mm, "end": v(168.86, 0.92) * mm});
            skLineSegment(sketch, "E275", {"start": v(168.86, 0.92) * mm, "end": v(167.77, 0.95) * mm});
            skLineSegment(sketch, "E276", {"start": v(167.77, 0.95) * mm, "end": v(166.46, 0.97) * mm});
            skLineSegment(sketch, "E277", {"start": v(166.46, 0.97) * mm, "end": v(165.34, 0.97) * mm});
            skLineSegment(sketch, "E278", {"start": v(165.34, 0.97) * mm, "end": v(164.22, 0.96) * mm});
            skLineSegment(sketch, "E279", {"start": v(164.22, 0.96) * mm, "end": v(163.36, 0.92) * mm});
            skLineSegment(sketch, "E280", {"start": v(163.36, 0.92) * mm, "end": v(162.59, 0.87) * mm});
            skLineSegment(sketch, "E281", {"start": v(162.59, 0.87) * mm, "end": v(161.76, 0.77) * mm});
            skLineSegment(sketch, "E282", {"start": v(161.76, 0.77) * mm, "end": v(161.16, 0.67) * mm});
            skLineSegment(sketch, "E283", {"start": v(161.16, 0.67) * mm, "end": v(160.67, 0.53) * mm});
            skLineSegment(sketch, "E284", {"start": v(160.67, 0.53) * mm, "end": v(160.3, 0.36) * mm});
            skLineSegment(sketch, "E285", {"start": v(160.3, 0.36) * mm, "end": v(160.11, 0.23) * mm});
            skLineSegment(sketch, "E286", {"start": v(160.11, 0.23) * mm, "end": v(160.02, 0.1) * mm});
            skLineSegment(sketch, "E287", {"start": v(160.02, 0.1) * mm, "end": v(160, 0) * mm});
            skLineSegment(sketch, "E288", {"start": v(160, 0) * mm, "end": v(160, -0.05) * mm});
            skLineSegment(sketch, "E289", {"start": v(160, -0.05) * mm, "end": v(160.02, -0.1) * mm});
            skLineSegment(sketch, "E290", {"start": v(160.02, -0.1) * mm, "end": v(160.05, -0.15) * mm});
            skLineSegment(sketch, "E291", {"start": v(160.05, -0.15) * mm, "end": v(160.23, -0.32) * mm});
            skLineSegment(sketch, "E292", {"start": v(160.23, -0.32) * mm, "end": v(160.48, -0.45) * mm});
            skLineSegment(sketch, "E293", {"start": v(160.48, -0.45) * mm, "end": v(160.86, -0.59) * mm});
            skLineSegment(sketch, "E294", {"start": v(160.86, -0.59) * mm, "end": v(161.46, -0.72) * mm});
            skLineSegment(sketch, "E295", {"start": v(161.46, -0.72) * mm, "end": v(162.16, -0.82) * mm});
            skLineSegment(sketch, "E296", {"start": v(162.16, -0.82) * mm, "end": v(163.04, -0.9) * mm});
            skLineSegment(sketch, "E297", {"start": v(163.04, -0.9) * mm, "end": v(164.05, -0.95) * mm});
            skLineSegment(sketch, "E298", {"start": v(164.05, -0.95) * mm, "end": v(165.23, -0.97) * mm});
            skLineSegment(sketch, "E299", {"start": v(165.23, -0.97) * mm, "end": v(166.5, -0.97) * mm});
            skLineSegment(sketch, "E300", {"start": v(166.5, -0.97) * mm, "end": v(167.85, -0.94) * mm});
            skLineSegment(sketch, "E301", {"start": v(167.85, -0.94) * mm, "end": v(169.27, -0.9) * mm});
            skLineSegment(sketch, "E302", {"start": v(169.27, -0.9) * mm, "end": v(170.78, -0.85) * mm});
            skLineSegment(sketch, "E303", {"start": v(170.78, -0.85) * mm, "end": v(172.35, -0.79) * mm});
            skLineSegment(sketch, "E304", {"start": v(172.35, -0.79) * mm, "end": v(174.12, -0.7) * mm});
            skLineSegment(sketch, "E305", {"start": v(174.12, -0.7) * mm, "end": v(175.62, -0.64) * mm});
            skLineSegment(sketch, "E306", {"start": v(175.62, -0.64) * mm, "end": v(177.14, -0.57) * mm});
            skLineSegment(sketch, "E307", {"start": v(177.14, -0.57) * mm, "end": v(178.8, -0.5) * mm});
            skLineSegment(sketch, "E308", {"start": v(178.8, -0.5) * mm, "end": v(180.34, -0.44) * mm});
            skLineSegment(sketch, "E309", {"start": v(180.34, -0.44) * mm, "end": v(181.84, -0.37) * mm});
            skLineSegment(sketch, "E310", {"start": v(181.84, -0.37) * mm, "end": v(183.25, -0.32) * mm});
            skLineSegment(sketch, "E311", {"start": v(183.25, -0.32) * mm, "end": v(184.56, -0.26) * mm});
            skLineSegment(sketch, "E312", {"start": v(184.56, -0.26) * mm, "end": v(185.78, -0.2) * mm});
            skLineSegment(sketch, "E313", {"start": v(185.78, -0.2) * mm, "end": v(186.8, -0.17) * mm});
            skLineSegment(sketch, "E314", {"start": v(186.8, -0.17) * mm, "end": v(187.72, -0.12) * mm});
            skLineSegment(sketch, "E315", {"start": v(187.72, -0.12) * mm, "end": v(188.48, -0.1) * mm});
            skLineSegment(sketch, "E316", {"start": v(188.48, -0.1) * mm, "end": v(189.13, -0.07) * mm});
            skLineSegment(sketch, "E317", {"start": v(189.13, -0.07) * mm, "end": v(189.59, -0.05) * mm});
            skLineSegment(sketch, "E318", {"start": v(189.59, -0.05) * mm, "end": v(190, -0.03) * mm});
            skLineSegment(sketch, "E319", {"start": v(190, -0.03) * mm, "end": v(190, 0.04) * mm});
            skSolve(sketch);
        }
        {
            var Q0;
            Q0=qCreatedBy(makeId("Top.planeOp"),FACE);
            cPlane(context, id + "F9", {"entities" : qUnion([Q0]), "cplaneType" : CPlaneType.OFFSET, "offset" : 280 * mm, "width" : 150 * mm, "height" : 150 * mm});
        }
        {
            var Q0;
            Q0=qCreatedBy(makeId("Top.planeOp"),FACE);
            cPlane(context, id + "F10", {"entities" : qUnion([Q0]), "cplaneType" : CPlaneType.OFFSET, "offset" : 330 * mm, "width" : 150 * mm, "height" : 150 * mm});
        }
        {
            var Q0;
            Q0=qCreatedBy(id+"F9.planeOp",FACE);
            var sketch = newSketch(context, id + "F11", { "sketchPlane" : qUnion([Q0])});
            skLineSegment(sketch, "E320", {"start": v(171.51, 0.12) * mm, "end": v(171.12, 0.1) * mm});
            skLineSegment(sketch, "E321", {"start": v(171.12, 0.1) * mm, "end": v(170.28, 0.16) * mm});
            skLineSegment(sketch, "E322", {"start": v(170.28, 0.16) * mm, "end": v(168.69, 0.21) * mm});
            skLineSegment(sketch, "E323", {"start": v(168.69, 0.21) * mm, "end": v(166.65, 0.31) * mm});
            skLineSegment(sketch, "E324", {"start": v(166.65, 0.31) * mm, "end": v(163.96, 0.42) * mm});
            skLineSegment(sketch, "E325", {"start": v(163.96, 0.42) * mm, "end": v(161.01, 0.54) * mm});
            skLineSegment(sketch, "E326", {"start": v(161.01, 0.54) * mm, "end": v(157.83, 0.68) * mm});
            skLineSegment(sketch, "E327", {"start": v(157.83, 0.68) * mm, "end": v(154.34, 0.81) * mm});
            skLineSegment(sketch, "E328", {"start": v(154.34, 0.81) * mm, "end": v(150.3, 1.02) * mm});
            skLineSegment(sketch, "E329", {"start": v(150.3, 1.02) * mm, "end": v(146.35, 1.15) * mm});
            skLineSegment(sketch, "E330", {"start": v(146.35, 1.15) * mm, "end": v(142.2, 1.35) * mm});
            skLineSegment(sketch, "E331", {"start": v(142.2, 1.35) * mm, "end": v(137.5, 1.54) * mm});
            skLineSegment(sketch, "E332", {"start": v(137.5, 1.54) * mm, "end": v(132.96, 1.72) * mm});
            skLineSegment(sketch, "E333", {"start": v(132.96, 1.72) * mm, "end": v(128.24, 1.92) * mm});
            skLineSegment(sketch, "E334", {"start": v(128.24, 1.92) * mm, "end": v(123.29, 2.17) * mm});
            skLineSegment(sketch, "E335", {"start": v(123.29, 2.17) * mm, "end": v(118.95, 2.33) * mm});
            skLineSegment(sketch, "E336", {"start": v(118.95, 2.33) * mm, "end": v(114.11, 2.55) * mm});
            skLineSegment(sketch, "E337", {"start": v(114.11, 2.55) * mm, "end": v(110.8, 2.68) * mm});
            skLineSegment(sketch, "E338", {"start": v(110.8, 2.68) * mm, "end": v(105.96, 2.85) * mm});
            skLineSegment(sketch, "E339", {"start": v(105.96, 2.85) * mm, "end": v(102.58, 2.94) * mm});
            skLineSegment(sketch, "E340", {"start": v(102.58, 2.94) * mm, "end": v(98.54, 3) * mm});
            skLineSegment(sketch, "E341", {"start": v(98.54, 3) * mm, "end": v(95.07, 3.02) * mm});
            skLineSegment(sketch, "E342", {"start": v(95.07, 3.02) * mm, "end": v(91.6, 2.97) * mm});
            skLineSegment(sketch, "E343", {"start": v(91.6, 2.97) * mm, "end": v(88.92, 2.86) * mm});
            skLineSegment(sketch, "E344", {"start": v(88.92, 2.86) * mm, "end": v(86.52, 2.68) * mm});
            skLineSegment(sketch, "E345", {"start": v(86.52, 2.68) * mm, "end": v(83.95, 2.39) * mm});
            skLineSegment(sketch, "E346", {"start": v(83.95, 2.39) * mm, "end": v(82.1, 2.06) * mm});
            skLineSegment(sketch, "E347", {"start": v(82.1, 2.06) * mm, "end": v(80.59, 1.63) * mm});
            skLineSegment(sketch, "E348", {"start": v(80.59, 1.63) * mm, "end": v(79.44, 1.12) * mm});
            skLineSegment(sketch, "E349", {"start": v(79.44, 1.12) * mm, "end": v(78.84, 0.7) * mm});
            skLineSegment(sketch, "E350", {"start": v(78.84, 0.7) * mm, "end": v(78.55, 0.29) * mm});
            skLineSegment(sketch, "E351", {"start": v(78.55, 0.29) * mm, "end": v(78.49, 0) * mm});
            skLineSegment(sketch, "E352", {"start": v(78.49, 0) * mm, "end": v(78.51, -0.16) * mm});
            skLineSegment(sketch, "E353", {"start": v(78.51, -0.16) * mm, "end": v(78.55, -0.33) * mm});
            skLineSegment(sketch, "E354", {"start": v(78.55, -0.33) * mm, "end": v(78.65, -0.48) * mm});
            skLineSegment(sketch, "E355", {"start": v(78.65, -0.48) * mm, "end": v(79.2, -0.99) * mm});
            skLineSegment(sketch, "E356", {"start": v(79.2, -0.99) * mm, "end": v(79.97, -1.38) * mm});
            skLineSegment(sketch, "E357", {"start": v(79.97, -1.38) * mm, "end": v(81.16, -1.81) * mm});
            skLineSegment(sketch, "E358", {"start": v(81.16, -1.81) * mm, "end": v(83.03, -2.24) * mm});
            skLineSegment(sketch, "E359", {"start": v(83.03, -2.24) * mm, "end": v(85.2, -2.55) * mm});
            skLineSegment(sketch, "E360", {"start": v(85.2, -2.55) * mm, "end": v(87.93, -2.8) * mm});
            skLineSegment(sketch, "E361", {"start": v(87.93, -2.8) * mm, "end": v(91.07, -2.96) * mm});
            skLineSegment(sketch, "E362", {"start": v(91.07, -2.96) * mm, "end": v(94.72, -3) * mm});
            skLineSegment(sketch, "E363", {"start": v(94.72, -3) * mm, "end": v(98.65, -3.02) * mm});
            skLineSegment(sketch, "E364", {"start": v(98.65, -3.02) * mm, "end": v(102.84, -2.9) * mm});
            skLineSegment(sketch, "E365", {"start": v(102.84, -2.9) * mm, "end": v(107.24, -2.78) * mm});
            skLineSegment(sketch, "E366", {"start": v(107.24, -2.78) * mm, "end": v(111.93, -2.63) * mm});
            skLineSegment(sketch, "E367", {"start": v(111.93, -2.63) * mm, "end": v(116.78, -2.44) * mm});
            skLineSegment(sketch, "E368", {"start": v(116.78, -2.44) * mm, "end": v(122.28, -2.17) * mm});
            skLineSegment(sketch, "E369", {"start": v(122.28, -2.17) * mm, "end": v(126.93, -1.98) * mm});
            skLineSegment(sketch, "E370", {"start": v(126.93, -1.98) * mm, "end": v(131.62, -1.78) * mm});
            skLineSegment(sketch, "E371", {"start": v(131.62, -1.78) * mm, "end": v(136.77, -1.55) * mm});
            skLineSegment(sketch, "E372", {"start": v(136.77, -1.55) * mm, "end": v(141.57, -1.36) * mm});
            skLineSegment(sketch, "E373", {"start": v(141.57, -1.36) * mm, "end": v(146.19, -1.16) * mm});
            skLineSegment(sketch, "E374", {"start": v(146.19, -1.16) * mm, "end": v(150.59, -0.98) * mm});
            skLineSegment(sketch, "E375", {"start": v(150.59, -0.98) * mm, "end": v(154.64, -0.8) * mm});
            skLineSegment(sketch, "E376", {"start": v(154.64, -0.8) * mm, "end": v(158.41, -0.65) * mm});
            skLineSegment(sketch, "E377", {"start": v(158.41, -0.65) * mm, "end": v(161.57, -0.52) * mm});
            skLineSegment(sketch, "E378", {"start": v(161.57, -0.52) * mm, "end": v(164.43, -0.39) * mm});
            skLineSegment(sketch, "E379", {"start": v(164.43, -0.39) * mm, "end": v(166.8, -0.3) * mm});
            skLineSegment(sketch, "E380", {"start": v(166.8, -0.3) * mm, "end": v(168.8, -0.2) * mm});
            skLineSegment(sketch, "E381", {"start": v(168.8, -0.2) * mm, "end": v(170.22, -0.14) * mm});
            skLineSegment(sketch, "E382", {"start": v(170.22, -0.14) * mm, "end": v(171.51, -0.1) * mm});
            skLineSegment(sketch, "E383", {"start": v(171.51, -0.1) * mm, "end": v(171.51, 0.12) * mm});
            skSolve(sketch);
        }
        {
            var Q0;
            Q0=qCreatedBy(id+"F10.planeOp",FACE);
            var sketch = newSketch(context, id + "F12", { "sketchPlane" : qUnion([Q0])});
            skLineSegment(sketch, "E384", {"start": v(184.5, 0.08) * mm, "end": v(184.23, 0.08) * mm});
            skLineSegment(sketch, "E385", {"start": v(184.23, 0.08) * mm, "end": v(183.64, 0.11) * mm});
            skLineSegment(sketch, "E386", {"start": v(183.64, 0.11) * mm, "end": v(182.53, 0.15) * mm});
            skLineSegment(sketch, "E387", {"start": v(182.53, 0.15) * mm, "end": v(181.1, 0.22) * mm});
            skLineSegment(sketch, "E388", {"start": v(181.1, 0.22) * mm, "end": v(179.23, 0.3) * mm});
            skLineSegment(sketch, "E389", {"start": v(179.23, 0.3) * mm, "end": v(177.16, 0.38) * mm});
            skLineSegment(sketch, "E390", {"start": v(177.16, 0.38) * mm, "end": v(174.94, 0.48) * mm});
            skLineSegment(sketch, "E391", {"start": v(174.94, 0.48) * mm, "end": v(172.5, 0.57) * mm});
            skLineSegment(sketch, "E392", {"start": v(172.5, 0.57) * mm, "end": v(169.68, 0.71) * mm});
            skLineSegment(sketch, "E393", {"start": v(169.68, 0.71) * mm, "end": v(166.92, 0.8) * mm});
            skLineSegment(sketch, "E394", {"start": v(166.92, 0.8) * mm, "end": v(164.02, 0.94) * mm});
            skLineSegment(sketch, "E395", {"start": v(164.02, 0.94) * mm, "end": v(160.73, 1.08) * mm});
            skLineSegment(sketch, "E396", {"start": v(160.73, 1.08) * mm, "end": v(157.56, 1.2) * mm});
            skLineSegment(sketch, "E397", {"start": v(157.56, 1.2) * mm, "end": v(154.26, 1.34) * mm});
            skLineSegment(sketch, "E398", {"start": v(154.26, 1.34) * mm, "end": v(150.8, 1.51) * mm});
            skLineSegment(sketch, "E399", {"start": v(150.8, 1.51) * mm, "end": v(147.77, 1.63) * mm});
            skLineSegment(sketch, "E400", {"start": v(147.77, 1.63) * mm, "end": v(144.4, 1.79) * mm});
            skLineSegment(sketch, "E401", {"start": v(144.4, 1.79) * mm, "end": v(142.08, 1.87) * mm});
            skLineSegment(sketch, "E402", {"start": v(142.08, 1.87) * mm, "end": v(138.7, 1.99) * mm});
            skLineSegment(sketch, "E403", {"start": v(138.7, 1.99) * mm, "end": v(136.33, 2.05) * mm});
            skLineSegment(sketch, "E404", {"start": v(136.33, 2.05) * mm, "end": v(133.5, 2.1) * mm});
            skLineSegment(sketch, "E405", {"start": v(133.5, 2.1) * mm, "end": v(131.08, 2.1) * mm});
            skLineSegment(sketch, "E406", {"start": v(131.08, 2.1) * mm, "end": v(128.66, 2.07) * mm});
            skLineSegment(sketch, "E407", {"start": v(128.66, 2.07) * mm, "end": v(126.79, 2) * mm});
            skLineSegment(sketch, "E408", {"start": v(126.79, 2) * mm, "end": v(125.1, 1.88) * mm});
            skLineSegment(sketch, "E409", {"start": v(125.1, 1.88) * mm, "end": v(123.31, 1.67) * mm});
            skLineSegment(sketch, "E410", {"start": v(123.31, 1.67) * mm, "end": v(122.03, 1.44) * mm});
            skLineSegment(sketch, "E411", {"start": v(122.03, 1.44) * mm, "end": v(120.96, 1.14) * mm});
            skLineSegment(sketch, "E412", {"start": v(120.96, 1.14) * mm, "end": v(120.16, 0.78) * mm});
            skLineSegment(sketch, "E413", {"start": v(120.16, 0.78) * mm, "end": v(119.75, 0.49) * mm});
            skLineSegment(sketch, "E414", {"start": v(119.75, 0.49) * mm, "end": v(119.54, 0.2) * mm});
            skLineSegment(sketch, "E415", {"start": v(119.54, 0.2) * mm, "end": v(119.5, 0) * mm});
            skLineSegment(sketch, "E416", {"start": v(119.5, 0) * mm, "end": v(119.51, -0.1) * mm});
            skLineSegment(sketch, "E417", {"start": v(119.51, -0.1) * mm, "end": v(119.54, -0.23) * mm});
            skLineSegment(sketch, "E418", {"start": v(119.54, -0.23) * mm, "end": v(119.61, -0.34) * mm});
            skLineSegment(sketch, "E419", {"start": v(119.61, -0.34) * mm, "end": v(120, -0.7) * mm});
            skLineSegment(sketch, "E420", {"start": v(120, -0.7) * mm, "end": v(120.54, -0.96) * mm});
            skLineSegment(sketch, "E421", {"start": v(120.54, -0.96) * mm, "end": v(121.37, -1.27) * mm});
            skLineSegment(sketch, "E422", {"start": v(121.37, -1.27) * mm, "end": v(122.67, -1.57) * mm});
            skLineSegment(sketch, "E423", {"start": v(122.67, -1.57) * mm, "end": v(124.18, -1.78) * mm});
            skLineSegment(sketch, "E424", {"start": v(124.18, -1.78) * mm, "end": v(126.1, -1.96) * mm});
            skLineSegment(sketch, "E425", {"start": v(126.1, -1.96) * mm, "end": v(128.29, -2.07) * mm});
            skLineSegment(sketch, "E426", {"start": v(128.29, -2.07) * mm, "end": v(130.84, -2.1) * mm});
            skLineSegment(sketch, "E427", {"start": v(130.84, -2.1) * mm, "end": v(133.59, -2.1) * mm});
            skLineSegment(sketch, "E428", {"start": v(133.59, -2.1) * mm, "end": v(136.51, -2.03) * mm});
            skLineSegment(sketch, "E429", {"start": v(136.51, -2.03) * mm, "end": v(139.6, -1.94) * mm});
            skLineSegment(sketch, "E430", {"start": v(139.6, -1.94) * mm, "end": v(142.87, -1.84) * mm});
            skLineSegment(sketch, "E431", {"start": v(142.87, -1.84) * mm, "end": v(146.26, -1.7) * mm});
            skLineSegment(sketch, "E432", {"start": v(146.26, -1.7) * mm, "end": v(150.1, -1.52) * mm});
            skLineSegment(sketch, "E433", {"start": v(150.1, -1.52) * mm, "end": v(153.35, -1.38) * mm});
            skLineSegment(sketch, "E434", {"start": v(153.35, -1.38) * mm, "end": v(156.63, -1.24) * mm});
            skLineSegment(sketch, "E435", {"start": v(156.63, -1.24) * mm, "end": v(160.22, -1.08) * mm});
            skLineSegment(sketch, "E436", {"start": v(160.22, -1.08) * mm, "end": v(163.58, -0.95) * mm});
            skLineSegment(sketch, "E437", {"start": v(163.58, -0.95) * mm, "end": v(166.8, -0.8) * mm});
            skLineSegment(sketch, "E438", {"start": v(166.8, -0.8) * mm, "end": v(169.88, -0.69) * mm});
            skLineSegment(sketch, "E439", {"start": v(169.88, -0.69) * mm, "end": v(172.7, -0.56) * mm});
            skLineSegment(sketch, "E440", {"start": v(172.7, -0.56) * mm, "end": v(175.35, -0.45) * mm});
            skLineSegment(sketch, "E441", {"start": v(175.35, -0.45) * mm, "end": v(177.55, -0.36) * mm});
            skLineSegment(sketch, "E442", {"start": v(177.55, -0.36) * mm, "end": v(179.55, -0.27) * mm});
            skLineSegment(sketch, "E443", {"start": v(179.55, -0.27) * mm, "end": v(181.2, -0.21) * mm});
            skLineSegment(sketch, "E444", {"start": v(181.2, -0.21) * mm, "end": v(182.61, -0.14) * mm});
            skLineSegment(sketch, "E445", {"start": v(182.61, -0.14) * mm, "end": v(183.6, -0.1) * mm});
            skLineSegment(sketch, "E446", {"start": v(183.6, -0.1) * mm, "end": v(184.5, -0.07) * mm});
            skLineSegment(sketch, "E447", {"start": v(184.5, -0.07) * mm, "end": v(184.5, 0.08) * mm});
            skSolve(sketch);
        }
        {
            var Q0;
            Q0 = qSketchRegion(id + "F4", true);
            var Q1;
            Q1 = qSketchRegion(id + "F5", true);
            var Q2;
            Q2 = qSketchRegion(id + "F11", true);
            var Q3;
            Q3 = qSketchRegion(id + "F6", true);
            var Q4;
            Q4 = qSketchRegion(id + "F7", true);
            var Q5;
            Q5 = qSketchRegion(id + "F12", true);
            var Q6;
            Q6 = qSketchRegion(id + "F8", true);
            loft(context, id + "F13", {"sheetProfilesArray" : [{ "sheetProfileEntities" : qUnion([Q0]) }, { "sheetProfileEntities" : qUnion([Q1]) }, { "sheetProfileEntities" : qUnion([Q2]) }, { "sheetProfileEntities" : qUnion([Q3]) }, { "sheetProfileEntities" : qUnion([Q4]) }, { "sheetProfileEntities" : qUnion([Q5]) }, { "sheetProfileEntities" : qUnion([Q6]) }]});
        }
    });
